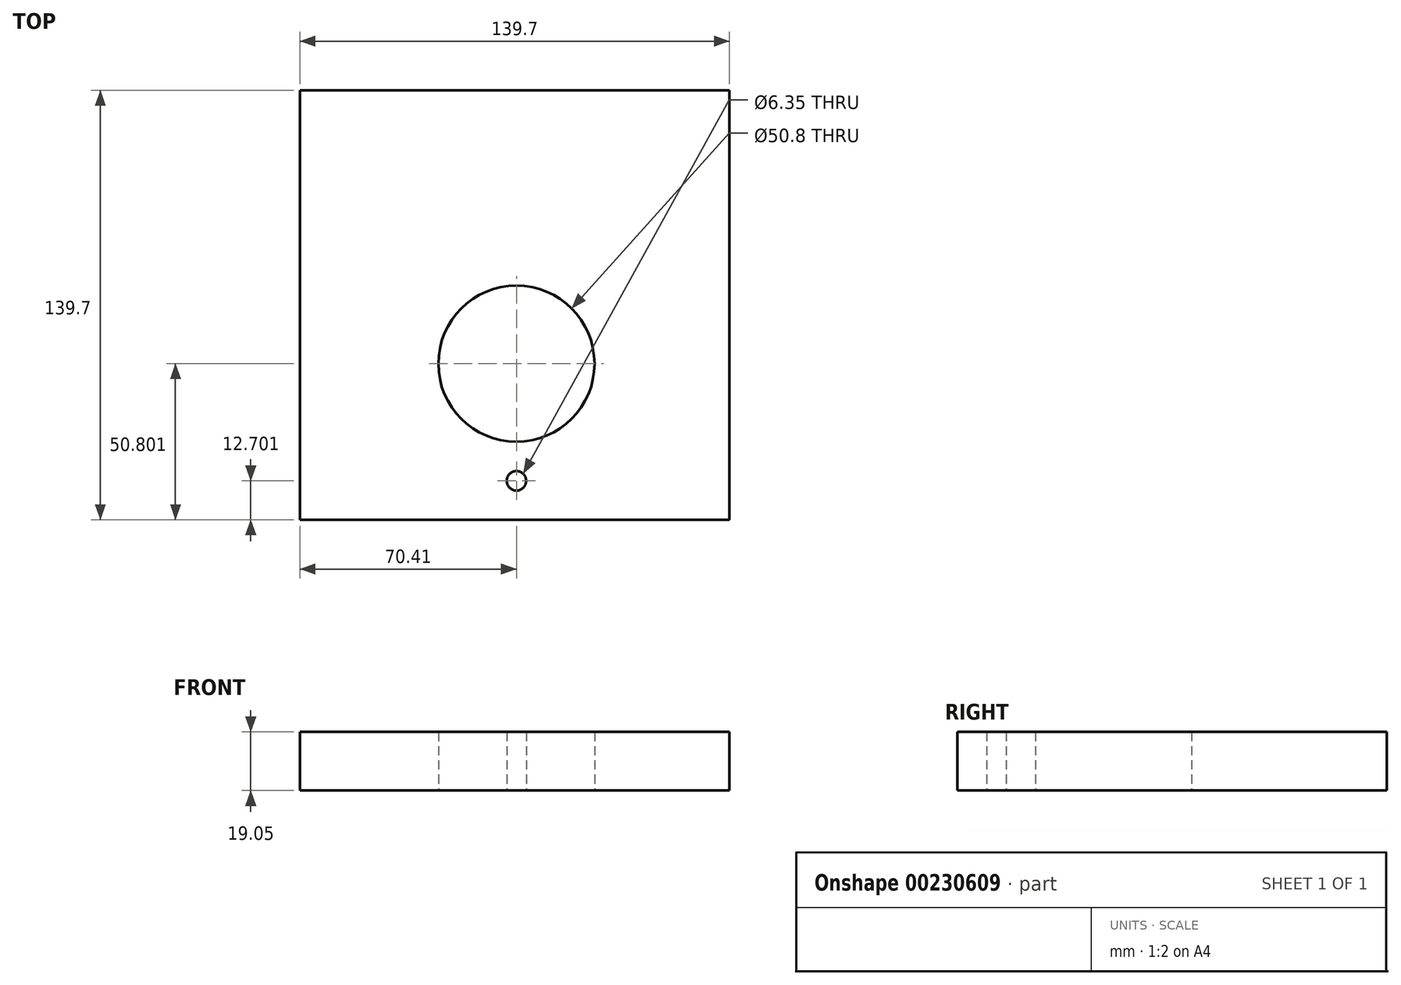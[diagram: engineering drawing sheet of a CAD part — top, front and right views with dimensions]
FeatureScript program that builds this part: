
annotation { "Feature Type Name" : "Feature", "Feature Type Description" : "" }
export const myFeature = defineFeature(function(context is Context, id is Id, definition is map)
    precondition{}
    {
        {
            var Q0;
            Q0=qCreatedBy(makeId("Top.planeOp"),FACE);
            var sketch = newSketch(context, id + "F0", { "sketchPlane" : qUnion([Q0])});
            skLineSegment(sketch, "E0.bottom", {"start": v(69.29, 70) * mm, "end": v(-70.41, 70) * mm});
            skLineSegment(sketch, "E0.top", {"start": v(69.29, -69.7) * mm, "end": v(-70.41, -69.7) * mm});
            skLineSegment(sketch, "E0.left", {"start": v(69.29, 70) * mm, "end": v(69.29, -69.7) * mm});
            skLineSegment(sketch, "E0.right", {"start": v(-70.41, 70) * mm, "end": v(-70.41, -69.7) * mm});
            skPoint(sketch, "E0.middle", {"position": v(-0.56, 0.14) * mm});
            skLineSegment(sketch, "E1", {"start": v(0, -69.7) * mm, "end": v(0, -57) * mm});
            skCircle(sketch, "E2", {"center": v(0, -57) * mm, "radius": 3.18 * mm});
            skLineSegment(sketch, "E3", {"start": v(0, -57) * mm, "end": v(0, -18.9) * mm});
            skCircle(sketch, "E4", {"center": v(0, -18.9) * mm, "radius": 25.4 * mm});
            skSolve(sketch);
        }
        {
            var Q0;
            Q0 = qSketchRegion(id + "F0", true);
            extrude(context, id + "F1", {"entities" : qUnion([Q0]), "depth" : 19.05 * mm});
        }
    });
